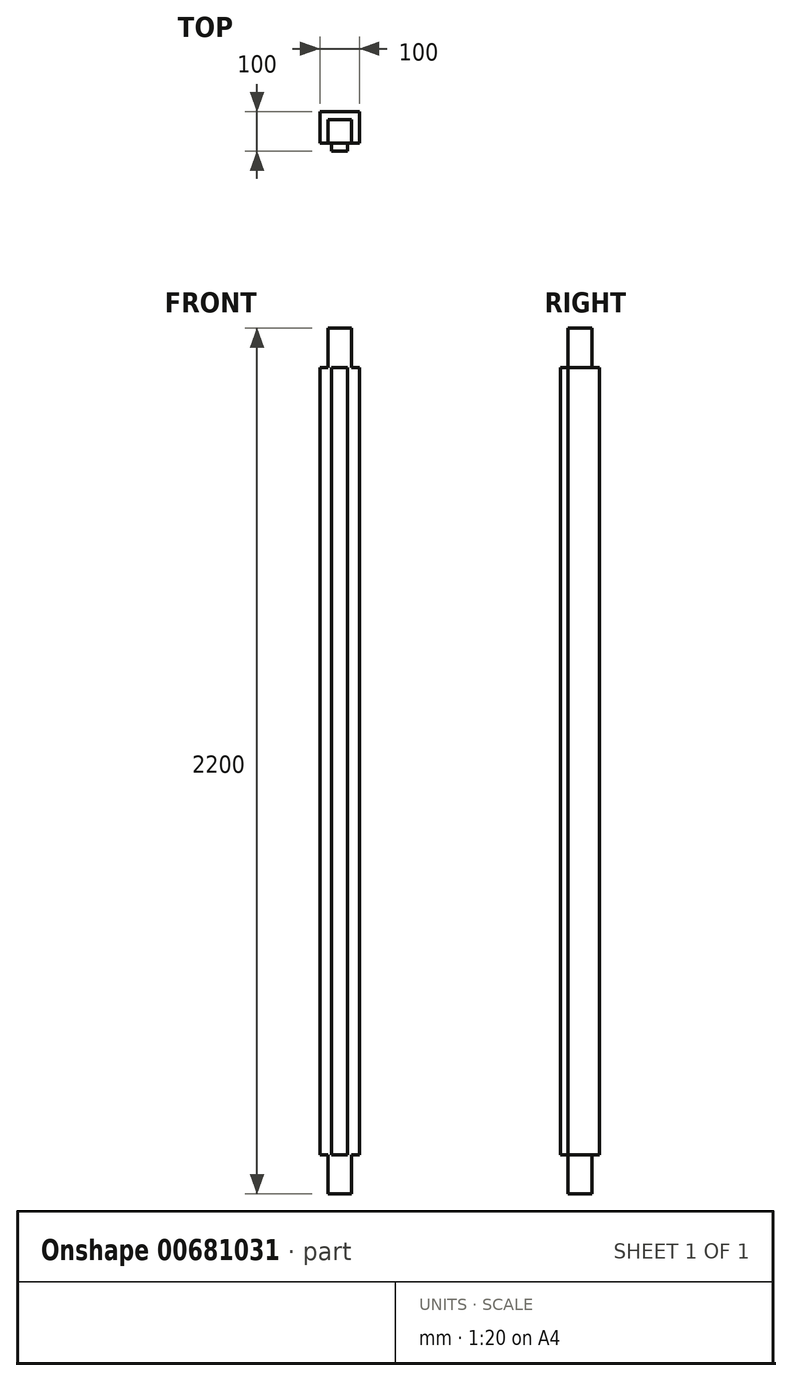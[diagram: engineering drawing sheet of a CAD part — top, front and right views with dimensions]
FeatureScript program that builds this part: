
annotation { "Feature Type Name" : "Feature", "Feature Type Description" : "" }
export const myFeature = defineFeature(function(context is Context, id is Id, definition is map)
    precondition{}
    {
        {
            var Q0;
            Q0=qCreatedBy(makeId("Front.planeOp"),FACE);
            var sketch = newSketch(context, id + "F0", { "sketchPlane" : qUnion([Q0])});
            skLineSegment(sketch, "E0.bottom", {"start": v(0, 0) * mm, "end": v(100, 0) * mm});
            skLineSegment(sketch, "E0.top", {"start": v(0, 2200) * mm, "end": v(100, 2200) * mm});
            skLineSegment(sketch, "E0.left", {"start": v(0, 0) * mm, "end": v(0, 2200) * mm});
            skLineSegment(sketch, "E0.right", {"start": v(100, 0) * mm, "end": v(100, 2200) * mm});
            skSolve(sketch);
        }
        {
            var Q0;
            Q0 = qSketchRegion(id + "F0", true);
            extrude(context, id + "F1", {"entities" : qUnion([Q0]), "depth" : 100 * mm, "offsetDistance" : 25 * mm});
        }
        {
            var Q0;
            Q0=makeQuery(id+"F1.opExtrude","CAP_FACE",FACE,{"disambiguationData":[OSD([sQuery(id+"F0.wireOp",EDGE,"E0.bottom"),sQuery(id+"F0.wireOp",EDGE,"E0.top"),sQuery(id+"F0.wireOp",EDGE,"E0.left"),sQuery(id+"F0.wireOp",EDGE,"E0.right")])],"isStart":false});
            var sketch = newSketch(context, id + "F2", { "sketchPlane" : qUnion([Q0])});
            skLineSegment(sketch, "E1.bottom", {"start": v(100, 0) * mm, "end": v(70, 0) * mm});
            skLineSegment(sketch, "E1.top", {"start": v(100, 2200) * mm, "end": v(70, 2200) * mm});
            skLineSegment(sketch, "E1.left", {"start": v(100, 0) * mm, "end": v(100, 2200) * mm});
            skLineSegment(sketch, "E1.right", {"start": v(70, 0) * mm, "end": v(70, 2200) * mm});
            skLineSegment(sketch, "E2.bottom", {"start": v(0, 0) * mm, "end": v(30, 0) * mm});
            skLineSegment(sketch, "E2.top", {"start": v(0, 2200) * mm, "end": v(30, 2200) * mm});
            skLineSegment(sketch, "E2.left", {"start": v(0, 0) * mm, "end": v(0, 2200) * mm});
            skLineSegment(sketch, "E2.right", {"start": v(30, 0) * mm, "end": v(30, 2200) * mm});
            skSolve(sketch);
        }
        {
            var Q0;
            Q0=makeQuery(id+"F2.imprint","IMPRINT",FACE,{"disambiguationData":[TD([[makeQuery(id+"F2.imprint","IMPRINT",EDGE,{"derivedFrom":sQuery(id+"F2.wireOp",EDGE,"E2.bottom")}),1.0]])]});
            var Q1;
            Q1=makeQuery(id+"F2.imprint","IMPRINT",FACE,{"disambiguationData":[TD([[makeQuery(id+"F2.imprint","IMPRINT",EDGE,{"derivedFrom":sQuery(id+"F2.wireOp",EDGE,"E1.bottom")}),1.0]])]});
            extrude(context, id + "F3", {"entities" : qUnion([Q0, Q1]), "operationType" : NewBodyOperationType.REMOVE, "oppositeDirection" : true, "depth" : 20 * mm, "offsetDistance" : 25 * mm});
        }
        {
            var Q0;
            Q0=makeQuery(id+"F1.opExtrude","SWEPT_FACE",FACE,{"disambiguationData":[OSD([sQuery(id+"F0.wireOp",EDGE,"E0.top")])]});
            var sketch = newSketch(context, id + "F4", { "sketchPlane" : qUnion([Q0])});
            skLineSegment(sketch, "E3.bottom", {"start": v(20, -20) * mm, "end": v(80, -20) * mm});
            skLineSegment(sketch, "E3.top", {"start": v(20, -80) * mm, "end": v(80, -80) * mm});
            skLineSegment(sketch, "E3.left", {"start": v(20, -20) * mm, "end": v(20, -80) * mm});
            skLineSegment(sketch, "E3.right", {"start": v(80, -20) * mm, "end": v(80, -80) * mm});
            skSolve(sketch);
        }
        {
            var Q0;
            Q0=makeQuery(id+"F4.imprint","IMPRINT",FACE,{"disambiguationData":[TD([[makeQuery(id+"F4.imprint","IMPRINT",EDGE,{"derivedFrom":sQuery(id+"F4.wireOp",EDGE,"E3.bottom")}),1.0]])]});
            var Q1;
            {var subQ1=sQuery(id+"F0.wireOp",EDGE,"E0.top");Q1=makeQuery(id+"F4.imprint","IMPRINT",FACE,{"disambiguationData":[TD([[makeQuery(id+"F4.imprint","IMPRINT",EDGE,{"derivedFrom":makeQuery(id+"F1.opExtrude","CAP_EDGE",EDGE,{"disambiguationData":[OSD([subQ1])],"isStart":false})}),1.0]])]});}
            extrude(context, id + "F5", {"entities" : qUnion([Q0, Q1]), "operationType" : NewBodyOperationType.REMOVE, "oppositeDirection" : true, "depth" : 100 * mm, "offsetDistance" : 25 * mm});
        }
        {
            var Q0;
            Q0=makeQuery(id+"F1.opExtrude","SWEPT_FACE",FACE,{"disambiguationData":[OSD([sQuery(id+"F0.wireOp",EDGE,"E0.bottom")])]});
            var sketch = newSketch(context, id + "F6", { "sketchPlane" : qUnion([Q0])});
            skLineSegment(sketch, "E4.bottom", {"start": v(80, 20) * mm, "end": v(20, 20) * mm});
            skLineSegment(sketch, "E4.top", {"start": v(80, 80) * mm, "end": v(20, 80) * mm});
            skLineSegment(sketch, "E4.left", {"start": v(80, 20) * mm, "end": v(80, 80) * mm});
            skLineSegment(sketch, "E4.right", {"start": v(20, 20) * mm, "end": v(20, 80) * mm});
            skSolve(sketch);
        }
        {
            var Q0;
            Q0=makeQuery(id+"F6.imprint","IMPRINT",FACE,{"disambiguationData":[TD([[makeQuery(id+"F6.imprint","IMPRINT",EDGE,{"derivedFrom":sQuery(id+"F6.wireOp",EDGE,"E4.bottom")}),1.0]])]});
            var Q1;
            {var subQ1=sQuery(id+"F0.wireOp",EDGE,"E0.bottom");Q1=makeQuery(id+"F6.imprint","IMPRINT",FACE,{"disambiguationData":[TD([[makeQuery(id+"F6.imprint","IMPRINT",EDGE,{"derivedFrom":makeQuery(id+"F1.opExtrude","CAP_EDGE",EDGE,{"disambiguationData":[OSD([subQ1])],"isStart":false})}),-1.0]])]});}
            extrude(context, id + "F7", {"entities" : qUnion([Q0, Q1]), "operationType" : NewBodyOperationType.REMOVE, "oppositeDirection" : true, "depth" : 100 * mm, "offsetDistance" : 25 * mm});
        }
    });
